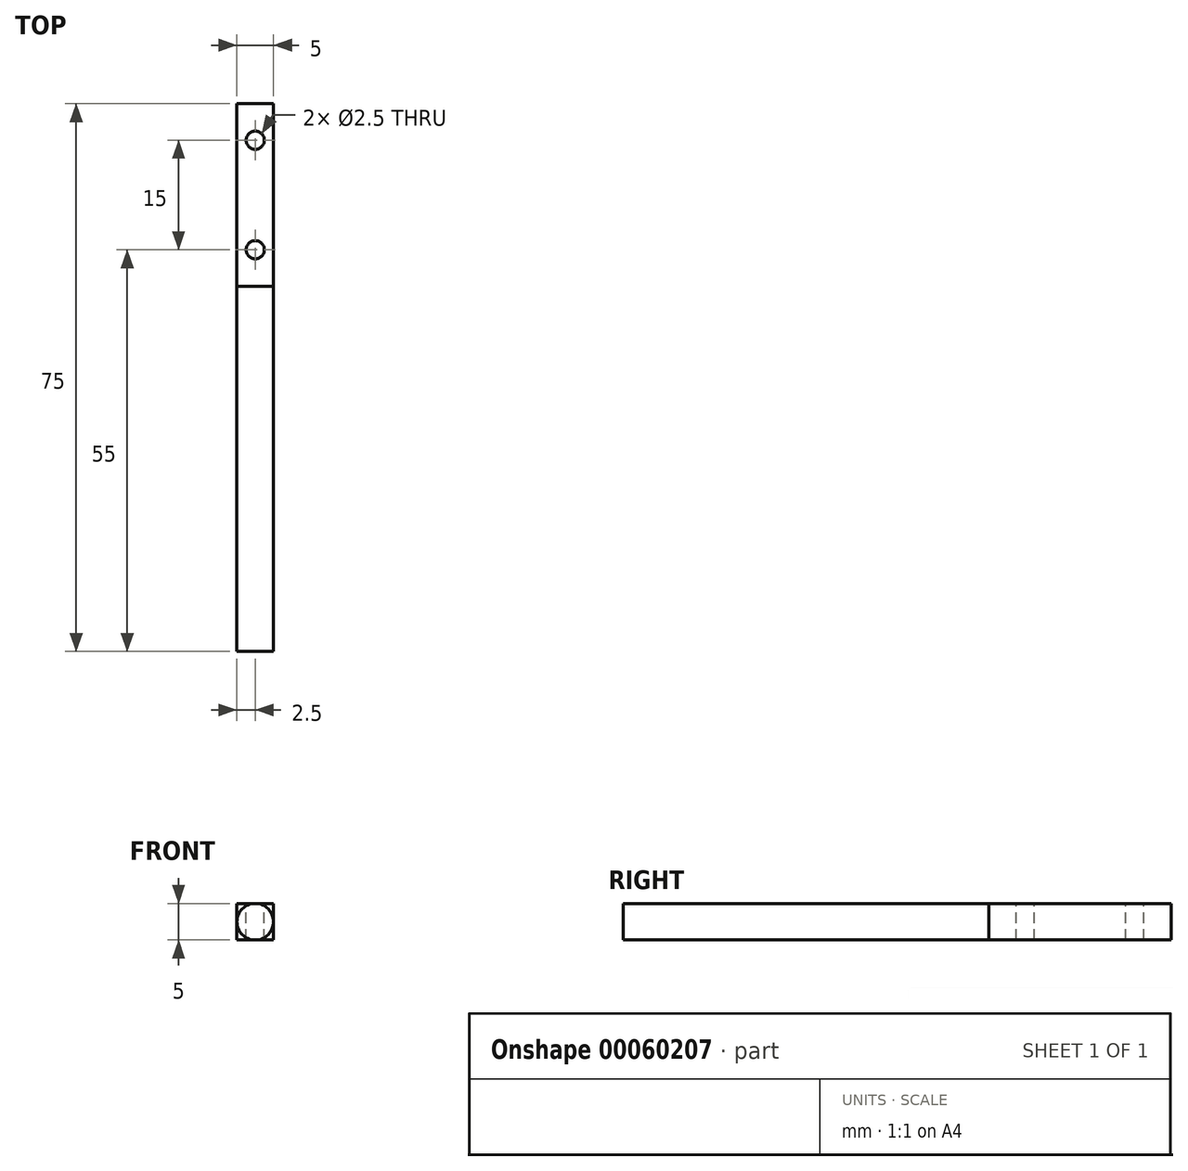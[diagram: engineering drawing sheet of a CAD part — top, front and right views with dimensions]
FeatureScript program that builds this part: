
annotation { "Feature Type Name" : "Feature", "Feature Type Description" : "" }
export const myFeature = defineFeature(function(context is Context, id is Id, definition is map)
    precondition{}
    {
        {
            var Q0;
            Q0=qCreatedBy(makeId("Front.planeOp"),FACE);
            var sketch = newSketch(context, id + "F0", { "sketchPlane" : qUnion([Q0])});
            skLineSegment(sketch, "E0.bottom", {"start": v(-2.5, 2.5) * mm, "end": v(2.5, 2.5) * mm});
            skLineSegment(sketch, "E0.top", {"start": v(-2.5, -2.5) * mm, "end": v(2.5, -2.5) * mm});
            skLineSegment(sketch, "E0.left", {"start": v(-2.5, 2.5) * mm, "end": v(-2.5, -2.5) * mm});
            skLineSegment(sketch, "E0.right", {"start": v(2.5, 2.5) * mm, "end": v(2.5, -2.5) * mm});
            skSolve(sketch);
        }
        {
            var Q0;
            Q0 = qSketchRegion(id + "F0", true);
            extrude(context, id + "F1", {"entities" : qUnion([Q0]), "depth" : 25 * mm});
        }
        {
            var Q0;
            Q0=makeQuery(id+"F1.opExtrude","CAP_FACE",FACE,{"disambiguationData":[OSD([sQuery(id+"F0.wireOp",EDGE,"E0.bottom"),sQuery(id+"F0.wireOp",EDGE,"E0.top"),sQuery(id+"F0.wireOp",EDGE,"E0.left"),sQuery(id+"F0.wireOp",EDGE,"E0.right")])],"isStart":false});
            var sketch = newSketch(context, id + "F2", { "sketchPlane" : qUnion([Q0])});
            skCircle(sketch, "E1", {"center": v(0, 0) * mm, "radius": 2.5 * mm});
            skSolve(sketch);
        }
        {
            var Q0;
            Q0 = qSketchRegion(id + "F2", true);
            extrude(context, id + "F3", {"entities" : qUnion([Q0]), "operationType" : NewBodyOperationType.ADD, "depth" : 50 * mm});
        }
        {
            var Q0;
            Q0=makeQuery(id+"F1.opExtrude","SWEPT_FACE",FACE,{"disambiguationData":[OSD([sQuery(id+"F0.wireOp",EDGE,"E0.bottom")])]});
            var sketch = newSketch(context, id + "F4", { "sketchPlane" : qUnion([Q0])});
            skCircle(sketch, "E2", {"center": v(0, -5) * mm, "radius": 1.25 * mm});
            skCircle(sketch, "E3", {"center": v(0, -20) * mm, "radius": 1.25 * mm});
            skSolve(sketch);
        }
        {
            var Q0;
            Q0 = qSketchRegion(id + "F4", true);
            extrude(context, id + "F5", {"entities" : qUnion([Q0]), "operationType" : NewBodyOperationType.REMOVE, "oppositeDirection" : true, "depth" : 25 * mm});
        }
    });
